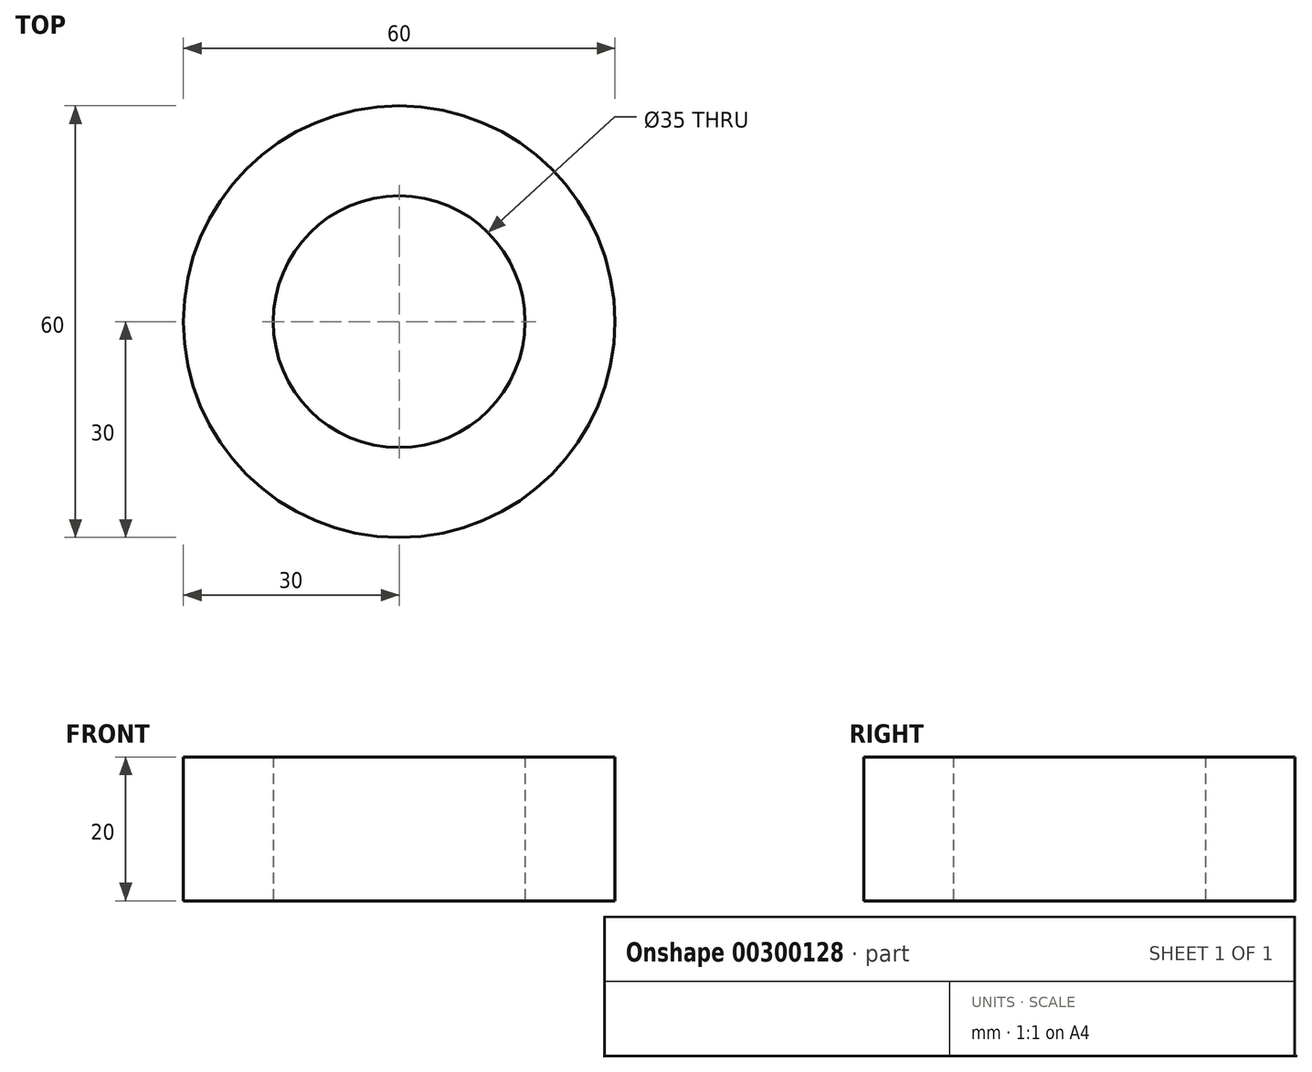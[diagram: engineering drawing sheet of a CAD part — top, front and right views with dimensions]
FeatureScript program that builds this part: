
annotation { "Feature Type Name" : "Feature", "Feature Type Description" : "" }
export const myFeature = defineFeature(function(context is Context, id is Id, definition is map)
    precondition{}
    {
        {
            var Q0;
            Q0=qCreatedBy(makeId("Top.planeOp"),FACE);
            var sketch = newSketch(context, id + "F0", { "sketchPlane" : qUnion([Q0])});
            skCircle(sketch, "E0", {"center": v(0, 0) * mm, "radius": 30 * mm});
            skCircle(sketch, "E1", {"center": v(0, 0) * mm, "radius": 17.5 * mm});
            skSolve(sketch);
        }
        {
            var Q0;
            Q0=makeQuery(id+"F0.imprint","IMPRINT",FACE,{"disambiguationData":[TD([[makeQuery(id+"F0.imprint","IMPRINT",EDGE,{"derivedFrom":sQuery(id+"F0.wireOp",EDGE,"E0")}),1.0]])]});
            extrude(context, id + "F1", {"entities" : qUnion([Q0]), "depth" : 20 * mm});
        }
    });
